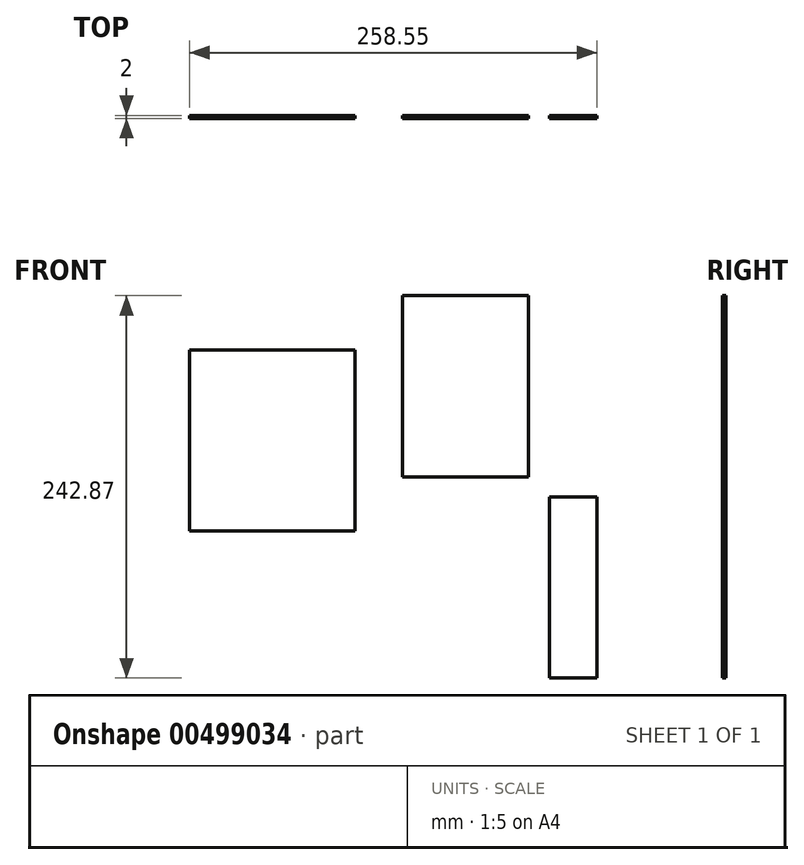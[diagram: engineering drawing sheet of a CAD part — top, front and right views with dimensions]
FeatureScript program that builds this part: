
annotation { "Feature Type Name" : "Feature", "Feature Type Description" : "" }
export const myFeature = defineFeature(function(context is Context, id is Id, definition is map)
    precondition{}
    {
        {
            var Q0;
            Q0=qCreatedBy(makeId("Front.planeOp"),FACE);
            var sketch = newSketch(context, id + "F0", { "sketchPlane" : qUnion([Q0])});
            skLineSegment(sketch, "E0.bottom", {"start": v(-124.25, 118.5) * mm, "end": v(-19.25, 118.5) * mm});
            skLineSegment(sketch, "E0.top", {"start": v(-124.25, 3.5) * mm, "end": v(-19.25, 3.5) * mm});
            skLineSegment(sketch, "E0.left", {"start": v(-124.25, 118.5) * mm, "end": v(-124.25, 3.5) * mm});
            skLineSegment(sketch, "E0.right", {"start": v(-19.25, 118.5) * mm, "end": v(-19.25, 3.5) * mm});
            skSolve(sketch);
        }
        {
            var Q0;
            Q0=makeQuery(id+"F0.imprint","IMPRINT",FACE,{"disambiguationData":[TD([[makeQuery(id+"F0.imprint","IMPRINT",EDGE,{"derivedFrom":sQuery(id+"F0.wireOp",EDGE,"E0.bottom")}),-1.0]])]});
            extrude(context, id + "F1", {"entities" : qUnion([Q0]), "depth" : 2 * mm});
        }
        {
            var Q0;
            Q0=qCreatedBy(makeId("Front.planeOp"),FACE);
            var sketch = newSketch(context, id + "F2", { "sketchPlane" : qUnion([Q0])});
            skLineSegment(sketch, "E1.bottom", {"start": v(10.9, 153.04) * mm, "end": v(90.9, 153.04) * mm});
            skLineSegment(sketch, "E1.top", {"start": v(10.9, 38.04) * mm, "end": v(90.9, 38.04) * mm});
            skLineSegment(sketch, "E1.left", {"start": v(10.9, 153.04) * mm, "end": v(10.9, 38.04) * mm});
            skLineSegment(sketch, "E1.right", {"start": v(90.9, 153.04) * mm, "end": v(90.9, 38.04) * mm});
            skSolve(sketch);
        }
        {
            var Q0;
            Q0=makeQuery(id+"F2.imprint","IMPRINT",FACE,{"disambiguationData":[TD([[makeQuery(id+"F2.imprint","IMPRINT",EDGE,{"derivedFrom":sQuery(id+"F2.wireOp",EDGE,"E1.bottom")}),-1.0]])]});
            extrude(context, id + "F3", {"entities" : qUnion([Q0]), "depth" : 2 * mm});
        }
        {
            var Q0;
            Q0=qCreatedBy(makeId("Front.planeOp"),FACE);
            var sketch = newSketch(context, id + "F4", { "sketchPlane" : qUnion([Q0])});
            skLineSegment(sketch, "E2.bottom", {"start": v(104.3, 25.17) * mm, "end": v(134.3, 25.17) * mm});
            skLineSegment(sketch, "E2.top", {"start": v(104.3, -89.83) * mm, "end": v(134.3, -89.83) * mm});
            skLineSegment(sketch, "E2.left", {"start": v(104.3, 25.17) * mm, "end": v(104.3, -89.83) * mm});
            skLineSegment(sketch, "E2.right", {"start": v(134.3, 25.17) * mm, "end": v(134.3, -89.83) * mm});
            skSolve(sketch);
        }
        {
            var Q0;
            Q0 = qSketchRegion(id + "F4", true);
            extrude(context, id + "F5", {"entities" : qUnion([Q0]), "operationType" : NewBodyOperationType.ADD, "depth" : 2 * mm});
        }
    });
